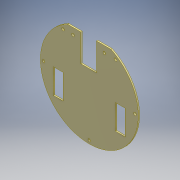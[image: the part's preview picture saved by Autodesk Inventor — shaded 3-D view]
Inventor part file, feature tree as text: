
AUTODESK INVENTOR PART (.ipt)
format: ipt  version: 2016 (Build 200138000, 138)  size: 148,480 bytes
history: native  units: mm
features: extrude x4, sketch x4, other x1
ambient origin geometry x8: Origin, YZ Plane, XZ Plane, XY Plane, X Axis, Y Axis, Z Axis, Center Point
bodies: Body1 (feature_tree)
feature tree (9):
  other  "Sólido1"
  extrude  "Extrusión1"  Depth=2.0mm TaperAngle=0.0deg
  extrude  "Extrusión2"  Depth=2.0mm
  extrude  "Extrusión3"  Depth=4.0mm
  extrude  "Extrusión4"  Depth=70.0mm
  sketch  "Boceto1"  dims[d0=150.0mm d1=18.0mm d2=25.0mm d3=15.0mm d4=38.0mm d5=15.0mm d6=38.0mm d7=40.0mm d8=40.0mm d9=2.0mm d10=0.0mm]
  sketch  "Boceto2"  dims[d11=2.0mm d12=0.0mm d13=5.0mm]
  sketch  "Boceto3"  dims[d14=4.0mm d15=4.0mm]
  sketch  "Boceto6"  dims[d16=4.0mm d17=70.0mm d18=70.0mm d19=70.0mm d20=6.0mm d21=0.0mm d22=4.0mm d23=4.0mm d24=4.0mm d25=4.0mm d26=6.0mm d27=0.0mm]
